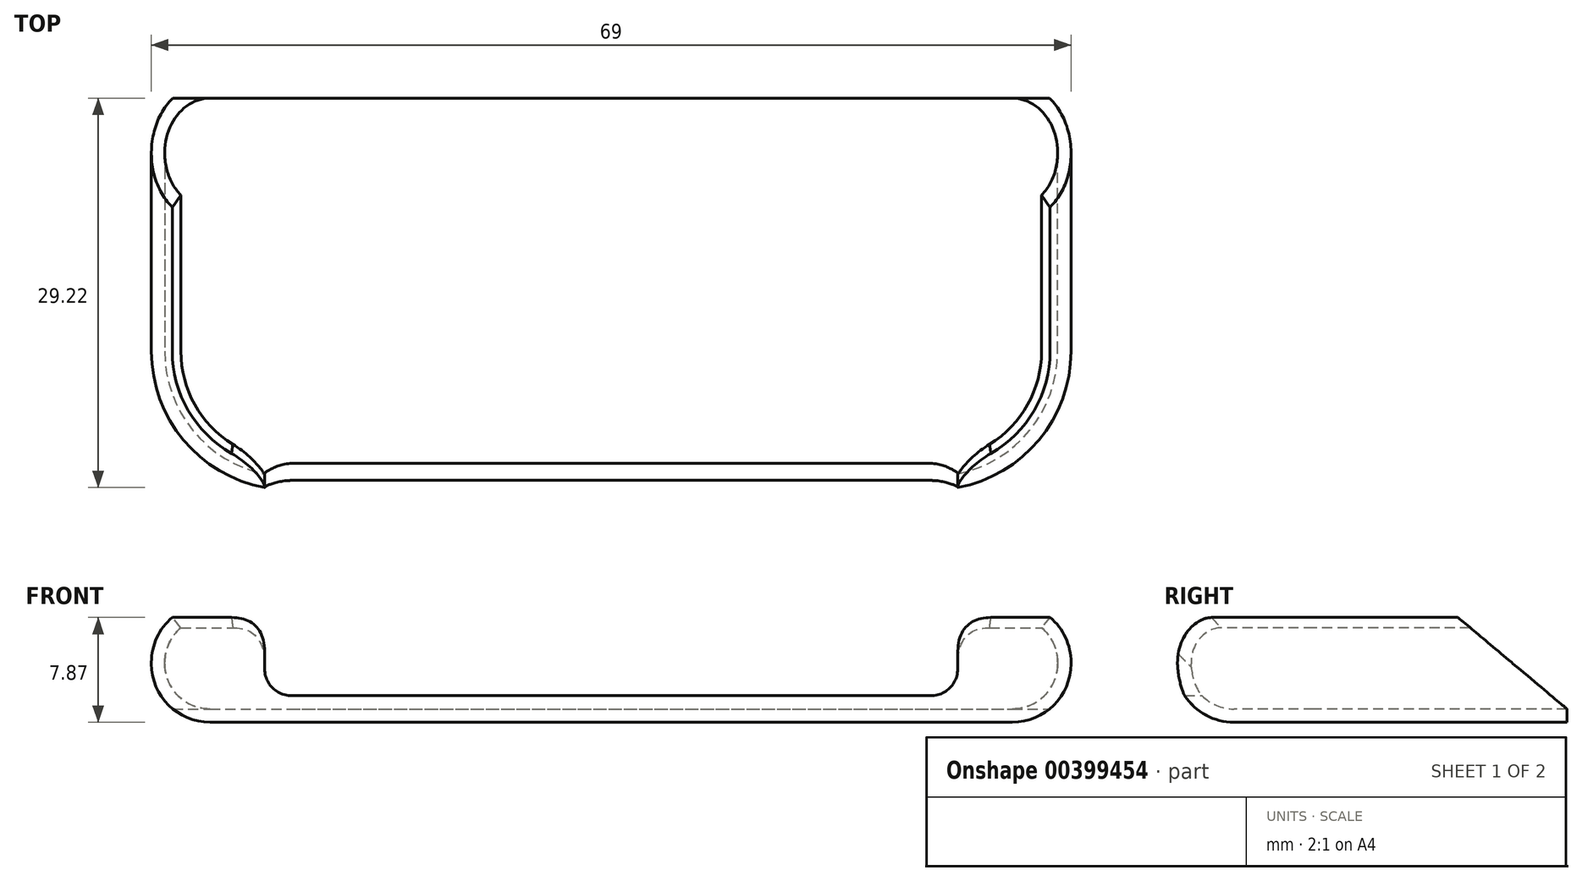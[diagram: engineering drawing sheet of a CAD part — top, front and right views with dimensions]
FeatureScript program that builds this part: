
annotation { "Feature Type Name" : "Feature", "Feature Type Description" : "" }
export const myFeature = defineFeature(function(context is Context, id is Id, definition is map)
    precondition{}
    {
        {
            var Q0;
            Q0=qCreatedBy(makeId("Top.planeOp"),FACE);
            var sketch = newSketch(context, id + "F0", { "sketchPlane" : qUnion([Q0])});
            skLineSegment(sketch, "E0.bottom", {"start": v(-30.1, 25) * mm, "end": v(30.1, 25) * mm});
            skLineSegment(sketch, "E0.top", {"start": v(-24.1, 0) * mm, "end": v(24.1, 0) * mm});
            skLineSegment(sketch, "E0.left", {"start": v(-30.1, 25) * mm, "end": v(-30.1, 6) * mm});
            skLineSegment(sketch, "E0.right", {"start": v(30.1, 25) * mm, "end": v(30.1, 6) * mm});
            skPoint(sketch, "E1.visualSharp", {"position": v(-30.1, 0) * mm});
            skArc(sketch, "E1.filletArc", {"start": v(-30.1, 6) * mm, "mid": v(-28.34, 1.76) * mm, "end": v(-24.1, 0) * mm});
            skPoint(sketch, "E2.visualSharp", {"position": v(30.1, 0) * mm});
            skArc(sketch, "E2.filletArc", {"start": v(24.1, 0) * mm, "mid": v(28.34, 1.76) * mm, "end": v(30.1, 6) * mm});
            skSolve(sketch);
        }
        {
            var Q0;
            Q0=makeQuery(id+"F0.imprint","IMPRINT",FACE,{"disambiguationData":[TD([[makeQuery(id+"F0.imprint","IMPRINT",EDGE,{"derivedFrom":sQuery(id+"F0.wireOp",EDGE,"E0.bottom")}),-1.0]])]});
            extrude(context, id + "F1", {"entities" : qUnion([Q0]), "depth" : 1 * mm});
        }
        {
            var Q0;
            Q0=makeQuery(id+"F1.opExtrude","SWEPT_FACE",FACE,{"disambiguationData":[OSD([sQuery(id+"F0.wireOp",EDGE,"E0.bottom")])]});
            var sketch = newSketch(context, id + "F2", { "sketchPlane" : qUnion([Q0])});
            skArc(sketch, "E3", {"start": v(30.1, 0) * mm, "mid": v(33.21, 1.29) * mm, "end": v(34.5, 4.4) * mm});
            skLineSegment(sketch, "E4", {"start": v(34.5, 4.5) * mm, "end": v(34.5, 4.4) * mm});
            skLineSegment(sketch, "E5", {"start": v(33.5, 4.5) * mm, "end": v(33.5, 4.4) * mm});
            skLineSegment(sketch, "E6", {"start": v(30.1, 4.5) * mm, "end": v(34.5, 4.5) * mm, "construction": true});
            skLineSegment(sketch, "E7.trimOffspring", {"start": v(32.3, 7.1) * mm, "end": v(32.93, 7.87) * mm});
            skArc(sketch, "E8.trimOffspring", {"start": v(33.5, 4.5) * mm, "mid": v(33.18, 5.93) * mm, "end": v(32.3, 7.1) * mm});
            skArc(sketch, "E9.trimOffspring", {"start": v(34.5, 4.5) * mm, "mid": v(34.09, 6.36) * mm, "end": v(32.93, 7.87) * mm});
            skLineSegment(sketch, "E10", {"start": v(30.1, 1) * mm, "end": v(30.1, 0) * mm});
            skArc(sketch, "E11.trimOffspring", {"start": v(30.1, 1) * mm, "mid": v(32.5, 2) * mm, "end": v(33.5, 4.4) * mm});
            skSolve(sketch);
        }
        {
            var Q0;
            Q0=makeQuery(id+"F2.imprint","IMPRINT",FACE,{"disambiguationData":[TD([[makeQuery(id+"F2.imprint","IMPRINT",EDGE,{"derivedFrom":sQuery(id+"F2.wireOp",EDGE,"t3hfqUgd-5InY-4kLa-6RaP-92Cpw2ne70uy")}),1.0]])]});
            var Q1;
            Q1=makeQuery(id+"F2.imprint","IMPRINT",FACE,{"disambiguationData":[TD([[makeQuery(id+"F2.imprint","IMPRINT",EDGE,{"derivedFrom":sQuery(id+"F2.wireOp",EDGE,"E3")}),1.0]])]});
            var Q2;
            Q2=makeQuery(id+"F1.opExtrude","CAP_EDGE",EDGE,{"disambiguationData":[OSD([sQuery(id+"F0.wireOp",EDGE,"E0.left")])],"isStart":false});
            var Q3;
            Q3=makeQuery(id+"F1.opExtrude","CAP_EDGE",EDGE,{"disambiguationData":[OSD([sQuery(id+"F0.wireOp",EDGE,"E1.filletArc")])],"isStart":false});
            var Q4;
            Q4=makeQuery(id+"F1.opExtrude","CAP_EDGE",EDGE,{"disambiguationData":[OSD([sQuery(id+"F0.wireOp",EDGE,"E0.top")])],"isStart":false});
            var Q5;
            Q5=makeQuery(id+"F1.opExtrude","CAP_EDGE",EDGE,{"disambiguationData":[OSD([sQuery(id+"F0.wireOp",EDGE,"E2.filletArc")])],"isStart":false});
            var Q6;
            Q6=makeQuery(id+"F1.opExtrude","CAP_EDGE",EDGE,{"disambiguationData":[OSD([sQuery(id+"F0.wireOp",EDGE,"E0.right")])],"isStart":false});
            sweep(context, id + "F3", {"operationType" : NewBodyOperationType.ADD, "profiles" : qUnion([Q0, Q1]), "path" : qUnion([Q2, Q3, Q4, Q5, Q6])});
        }
        {
            var Q0;
            {var subQ0=sQuery(id+"F2.wireOp",EDGE,"E11.trimOffspring");var subQ1=sQuery(id+"F2.wireOp",EDGE,"E10");var subQ2=sQuery(id+"F2.wireOp",EDGE,"E9.trimOffspring");var subQ3=sQuery(id+"F2.wireOp",EDGE,"E8.trimOffspring");var subQ4=sQuery(id+"F2.wireOp",EDGE,"E7.trimOffspring");var subQ5=sQuery(id+"F2.wireOp",EDGE,"E5");var subQ6=sQuery(id+"F2.wireOp",EDGE,"E4");var subQ7=sQuery(id+"F2.wireOp",EDGE,"E3");var subQ8=sQuery(id+"F0.wireOp",EDGE,"E0.bottom");Q0=makeQuery(id+"F3.boolean.opBoolean","MERGE",FACE,{"derivedFrom":[makeQuery(id+"F1.opExtrude","SWEPT_FACE",FACE,{"disambiguationData":[OSD([subQ8])]}),makeQuery(id+"F3.opSweep","CAP_FACE",FACE,{"disambiguationData":[OSD([subQ8,sQuery(id+"F0.wireOp",EDGE,"E0.left"),subQ7,subQ6,subQ5,subQ4,subQ3,subQ2,subQ1,subQ0])],"isStart":true}),makeQuery(id+"F3.opSweep","CAP_FACE",FACE,{"disambiguationData":[OSD([subQ8,sQuery(id+"F0.wireOp",EDGE,"E0.right"),subQ7,subQ6,subQ5,subQ4,subQ3,subQ2,subQ1,subQ0])],"isStart":false})]});}
            var sketch = newSketch(context, id + "F4", { "sketchPlane" : qUnion([Q0])});
            skLineSegment(sketch, "E12.bottom", {"start": v(-26, 7.87) * mm, "end": v(26, 7.87) * mm});
            skLineSegment(sketch, "E12.top", {"start": v(-24, 2) * mm, "end": v(24, 2) * mm});
            skLineSegment(sketch, "E12.left", {"start": v(-26, 7.87) * mm, "end": v(-26, 4) * mm});
            skLineSegment(sketch, "E12.right", {"start": v(26, 7.87) * mm, "end": v(26, 4) * mm});
            skPoint(sketch, "E13.visualSharp", {"position": v(-26, 2) * mm});
            skArc(sketch, "E13.filletArc", {"start": v(-26, 4) * mm, "mid": v(-25.41, 2.59) * mm, "end": v(-24, 2) * mm});
            skPoint(sketch, "E14.visualSharp", {"position": v(26, 2) * mm});
            skArc(sketch, "E14.filletArc", {"start": v(24, 2) * mm, "mid": v(25.41, 2.59) * mm, "end": v(26, 4) * mm});
            skSolve(sketch);
        }
        {
            var Q0;
            Q0=makeQuery(id+"F4.imprint","IMPRINT",FACE,{"disambiguationData":[TD([[makeQuery(id+"F4.imprint","IMPRINT",EDGE,{"derivedFrom":sQuery(id+"F4.wireOp",EDGE,"E12.bottom")}),-1.0]])]});
            extrude(context, id + "F5", {"entities" : qUnion([Q0]), "operationType" : NewBodyOperationType.REMOVE, "endBound" : BoundingType.THROUGH_ALL, "oppositeDirection" : true, "depth" : 25 * mm});
        }
        {
            var Q0;
            Q0=qCreatedBy(makeId("Right.planeOp"),FACE);
            var sketch = newSketch(context, id + "F6", { "sketchPlane" : qUnion([Q0])});
            skLineSegment(sketch, "E15", {"start": v(25, 1) * mm, "end": v(16.82, 7.87) * mm});
            skLineSegment(sketch, "E16", {"start": v(16.82, 7.87) * mm, "end": v(25, 7.87) * mm});
            skLineSegment(sketch, "E17", {"start": v(25, 7.87) * mm, "end": v(25, 1) * mm});
            skSolve(sketch);
        }
        {
            var Q0;
            Q0 = qSketchRegion(id + "F6", true);
            extrude(context, id + "F7", {"entities" : qUnion([Q0]), "operationType" : NewBodyOperationType.REMOVE, "endBound" : BoundingType.SYMMETRIC, "oppositeDirection" : true, "depth" : 500 * mm});
        }
        {
            var Q0;
            Q0=makeQuery(id+"F5.boolean.opBoolean","INTERSECT",EDGE,{"derivedFrom":[makeQuery(id+"F3.opSweep","SWEPT_FACE",FACE,{"disambiguationData":[OSD([sQuery(id+"F0.wireOp",EDGE,"E1.filletArc"),sQuery(id+"F2.wireOp",EDGE,"E7.trimOffspring")])]}),makeQuery(id+"F5.opExtrude","SWEPT_FACE",FACE,{"disambiguationData":[OSD([sQuery(id+"F4.wireOp",EDGE,"E12.right")])]})]});
            var Q1;
            Q1=makeQuery(id+"F5.boolean.opBoolean","INTERSECT",EDGE,{"derivedFrom":[makeQuery(id+"F3.opSweep","SWEPT_FACE",FACE,{"disambiguationData":[OSD([sQuery(id+"F0.wireOp",EDGE,"E2.filletArc"),sQuery(id+"F2.wireOp",EDGE,"E7.trimOffspring")])]}),makeQuery(id+"F5.opExtrude","SWEPT_FACE",FACE,{"disambiguationData":[OSD([sQuery(id+"F4.wireOp",EDGE,"E12.left")])]})]});
            fillet(context, id + "F8", {"entities" : qUnion([Q0, Q1]), "radius" : 4 * mm, "tangentPropagation" : true, "allowEdgeOverflow" : false});
        }
    });
